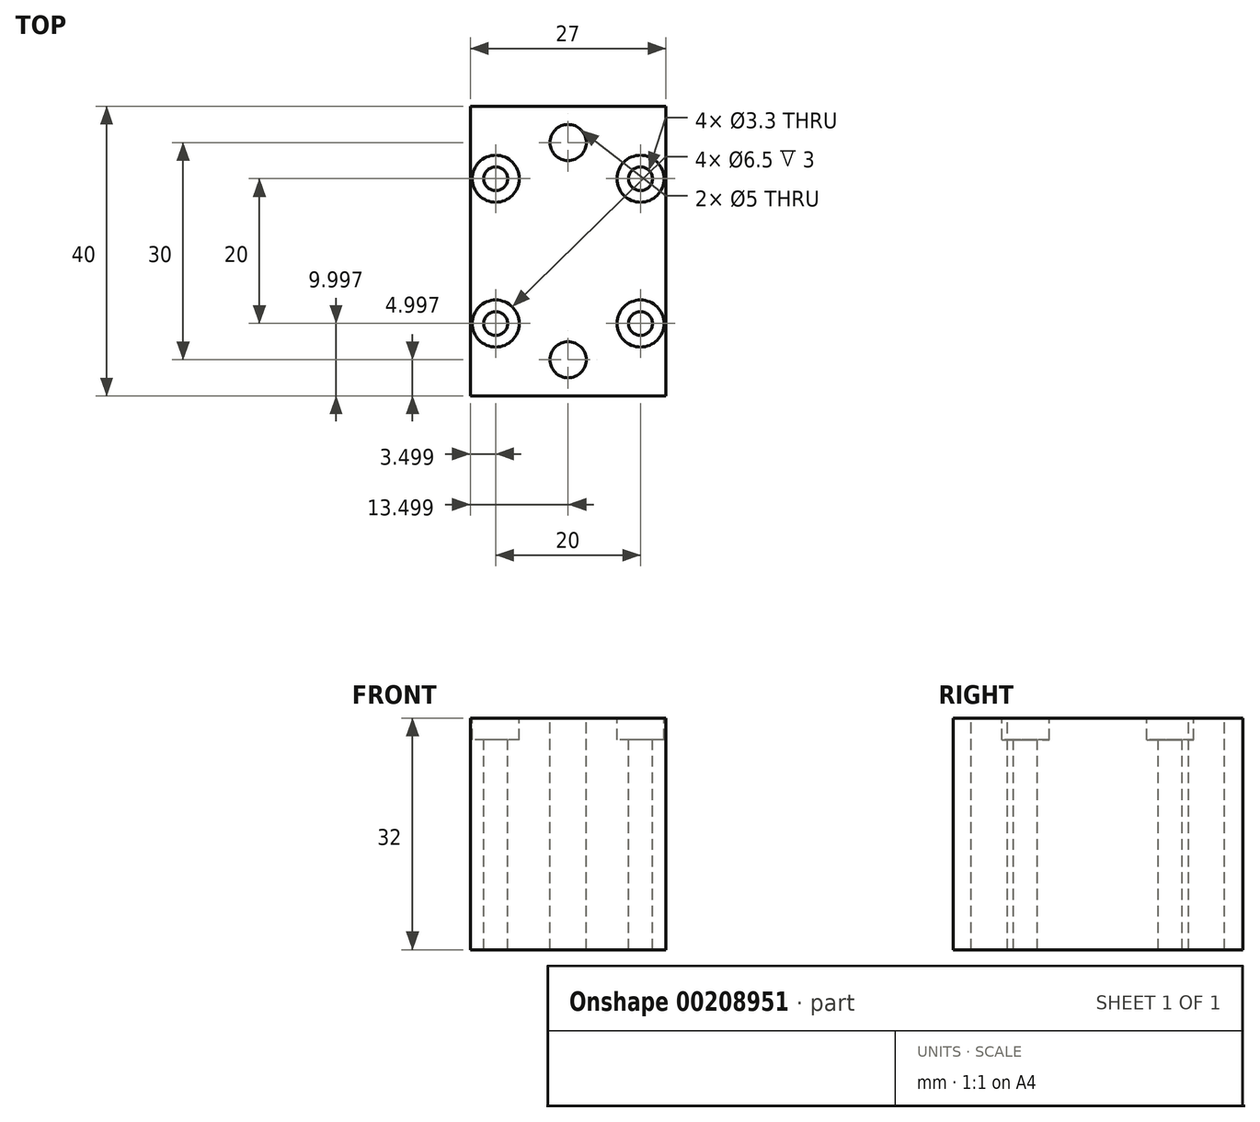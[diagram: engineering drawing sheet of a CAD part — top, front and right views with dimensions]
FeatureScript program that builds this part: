
annotation { "Feature Type Name" : "Feature", "Feature Type Description" : "" }
export const myFeature = defineFeature(function(context is Context, id is Id, definition is map)
    precondition{}
    {
        {
            var Q0;
            Q0=qCreatedBy(makeId("Top.planeOp"),FACE);
            var sketch = newSketch(context, id + "F0", { "sketchPlane" : qUnion([Q0])});
            skLineSegment(sketch, "E0.bottom", {"start": v(-36.8, -23.83) * mm, "end": v(-9.8, -23.83) * mm});
            skLineSegment(sketch, "E0.top", {"start": v(-36.8, -63.83) * mm, "end": v(-9.8, -63.83) * mm});
            skLineSegment(sketch, "E0.left", {"start": v(-36.8, -23.83) * mm, "end": v(-36.8, -63.83) * mm});
            skLineSegment(sketch, "E0.right", {"start": v(-9.8, -23.83) * mm, "end": v(-9.8, -63.83) * mm});
            skSolve(sketch);
        }
        {
            var Q0;
            Q0=makeQuery(id+"F0.imprint","IMPRINT",FACE,{"disambiguationData":[TD([[makeQuery(id+"F0.imprint","IMPRINT",EDGE,{"derivedFrom":sQuery(id+"F0.wireOp",EDGE,"E0.bottom")}),-1.0]])]});
            extrude(context, id + "F1", {"entities" : qUnion([Q0]), "depth" : 32 * mm});
        }
        {
            var Q0;
            Q0=makeQuery(id+"F1.opExtrude","CAP_FACE",FACE,{"disambiguationData":[OSD([sQuery(id+"F0.wireOp",EDGE,"E0.bottom"),sQuery(id+"F0.wireOp",EDGE,"E0.top"),sQuery(id+"F0.wireOp",EDGE,"E0.left"),sQuery(id+"F0.wireOp",EDGE,"E0.right")])],"isStart":false});
            var sketch = newSketch(context, id + "F2", { "sketchPlane" : qUnion([Q0])});
            skLineSegment(sketch, "E1", {"start": v(-23.3, -23.83) * mm, "end": v(-23.3, -63.83) * mm, "construction": true});
            skLineSegment(sketch, "E2", {"start": v(-36.8, -43.83) * mm, "end": v(-9.8, -43.83) * mm, "construction": true});
            skLineSegment(sketch, "E3.top", {"start": v(-23.3, -33.83) * mm, "end": v(-33.3, -33.83) * mm, "construction": true});
            skLineSegment(sketch, "E3.right", {"start": v(-33.3, -43.83) * mm, "end": v(-33.3, -33.83) * mm, "construction": true});
            skLineSegment(sketch, "E4.MirrorCS", {"start": v(-23.3, -33.83) * mm, "end": v(-13.3, -33.83) * mm, "construction": true});
            skLineSegment(sketch, "E5.MirrorCS", {"start": v(-13.3, -43.83) * mm, "end": v(-13.3, -33.83) * mm, "construction": true});
            skLineSegment(sketch, "E6.MirrorCS", {"start": v(-13.3, -43.83) * mm, "end": v(-13.3, -53.83) * mm, "construction": true});
            skLineSegment(sketch, "E7.MirrorCS", {"start": v(-23.3, -53.83) * mm, "end": v(-13.3, -53.83) * mm, "construction": true});
            skLineSegment(sketch, "E8.MirrorCS", {"start": v(-23.3, -53.83) * mm, "end": v(-33.3, -53.83) * mm, "construction": true});
            skLineSegment(sketch, "E9.MirrorCS", {"start": v(-33.3, -43.83) * mm, "end": v(-33.3, -53.83) * mm, "construction": true});
            skPoint(sketch, "E10", {"position": v(-23.3, -28.83) * mm});
            skPoint(sketch, "E11.MirrorP", {"position": v(-23.3, -58.83) * mm});
            skSolve(sketch);
        }
        {
            var Q0;
            Q0=sQuery(id+"F2.wireOp",VERTEX,"E3.top.end");
            var Q1;
            Q1=sQuery(id+"F2.wireOp",VERTEX,"E5.MirrorCS.end");
            var Q2;
            Q2=sQuery(id+"F2.wireOp",VERTEX,"E6.MirrorCS.end");
            var Q3;
            Q3=sQuery(id+"F2.wireOp",VERTEX,"E8.MirrorCS.end");
            var Q4;
            Q4=makeQuery(id+"F1.opExtrude","SWEPT_BODY",BODY,{"disambiguationData":[OSD([sQuery(id+"F0.wireOp",EDGE,"E0.bottom"),sQuery(id+"F0.wireOp",EDGE,"E0.top"),sQuery(id+"F0.wireOp",EDGE,"E0.left"),sQuery(id+"F0.wireOp",EDGE,"E0.right")])]});
            hole(context, id + "F3", {"style" : HoleStyle.C_BORE, "endStyle" : HoleEndStyle.THROUGH, "standardTappedOrClearance" : lookupTablePath({ "standard" : "ISO", "fit" : "Normal", "size" : "M3", "type" : "Clearance" }), "standardBlindInLast" : lookupTablePath({ "fit" : "Standard", "standard" : "ISO", "size" : "M3", "type" : "Clearance" }), "holeDiameter" : 3.3 * mm, "cBoreDiameter" : 6.5 * mm, "cBoreDepth" : 3 * mm, "locations" : qUnion([Q0, Q1, Q2, Q3]), "scope" : qUnion([Q4]), "isTappedThrough" : true});
        }
        {
            var Q0;
            Q0=sQuery(id+"F2.wireOp",VERTEX,"E10");
            var Q1;
            Q1=sQuery(id+"F2.wireOp",VERTEX,"E11.MirrorP");
            var Q2;
            Q2=makeQuery(id+"F1.opExtrude","SWEPT_BODY",BODY,{"disambiguationData":[OSD([sQuery(id+"F0.wireOp",EDGE,"E0.bottom"),sQuery(id+"F0.wireOp",EDGE,"E0.top"),sQuery(id+"F0.wireOp",EDGE,"E0.left"),sQuery(id+"F0.wireOp",EDGE,"E0.right")])]});
            hole(context, id + "F4", {"style" : HoleStyle.SIMPLE, "endStyle" : HoleEndStyle.THROUGH, "standardTappedOrClearance" : lookupTablePath({ "standard" : "ISO", "engagement" : "75%", "pitch" : "1 mm", "size" : "M6", "type" : "Tapped" }), "standardBlindInLast" : lookupTablePath({ "standard" : "ISO", "engagement" : "75%", "pitch" : "1 mm", "size" : "M6", "type" : "Tapped" }), "holeDiameter" : 5 * mm, "locations" : qUnion([Q0, Q1]), "scope" : qUnion([Q2]), "isTappedThrough" : true, "majorDiameter" : 6 * mm, "showTappedDepth" : true});
        }
    });
